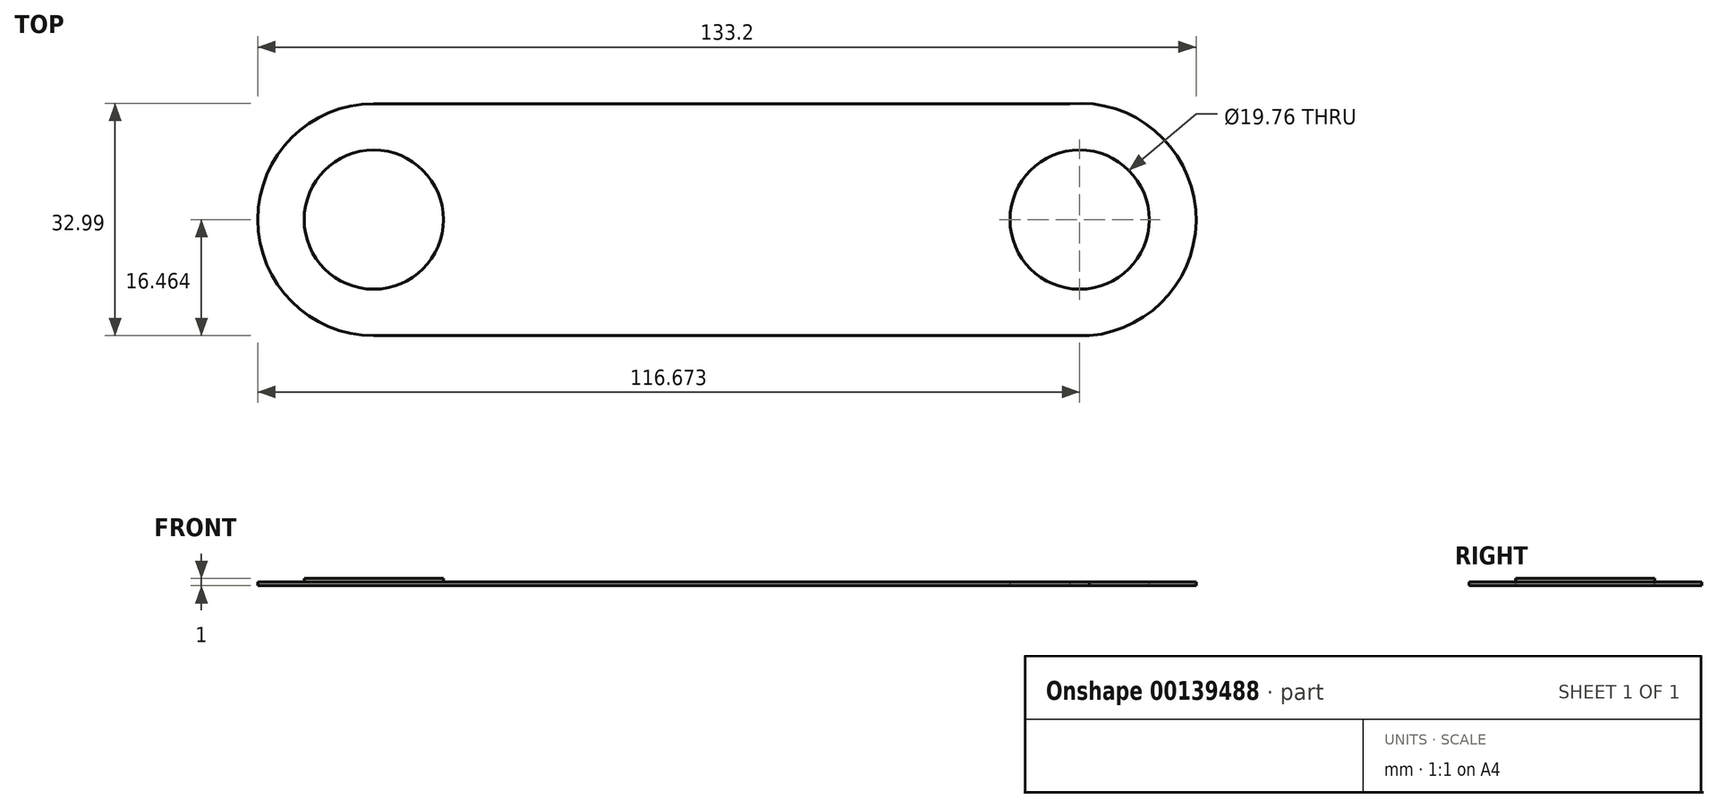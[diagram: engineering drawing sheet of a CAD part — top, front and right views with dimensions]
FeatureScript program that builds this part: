
annotation { "Feature Type Name" : "Feature", "Feature Type Description" : "" }
export const myFeature = defineFeature(function(context is Context, id is Id, definition is map)
    precondition{}
    {
        {
            assignVariable(context, id + "F0", {"name" : "Depth", "anyValue" : .5});
        }
        {
            var Q0;
            Q0=qCreatedBy(makeId("Top.planeOp"),FACE);
            var sketch = newSketch(context, id + "F1", { "sketchPlane" : qUnion([Q0])});
            skLineSegment(sketch, "E0.bottom", {"start": v(48, 16) * mm, "end": v(-50.8, 16) * mm});
            skLineSegment(sketch, "E0.top", {"start": v(50.8, -16.93) * mm, "end": v(-50.8, -16.93) * mm});
            skPoint(sketch, "E0.middle", {"position": v(0, 0) * mm});
            skArc(sketch, "E1", {"start": v(-50.8, 16) * mm, "mid": v(-67.27, -0.47) * mm, "end": v(-50.8, -16.93) * mm});
            skArc(sketch, "E2", {"start": v(48, 16) * mm, "mid": v(65.87, 0.93) * mm, "end": v(50.8, -16.93) * mm});
            skSolve(sketch);
        }
        {
            var Q0;
            Q0 = qSketchRegion(id + "F1", true);
            extrude(context, id + "F2", {"entities" : qUnion([Q0]), "depth" : (getVariable(context, 'Depth')) * mm});
        }
        {
            var Q0;
            Q0=makeQuery(id+"F2.opExtrude","CAP_FACE",FACE,{"disambiguationData":[OSD([sQuery(id+"F1.wireOp",EDGE,"E0.bottom"),sQuery(id+"F1.wireOp",EDGE,"E0.top"),sQuery(id+"F1.wireOp",EDGE,"E1"),sQuery(id+"F1.wireOp",EDGE,"E2")])],"isStart":false});
            var sketch = newSketch(context, id + "F3", { "sketchPlane" : qUnion([Q0])});
            skCircle(sketch, "E3", {"center": v(-50.8, -0.47) * mm, "radius": 9.88 * mm});
            skCircle(sketch, "E4", {"center": v(49.4, -0.47) * mm, "radius": 9.88 * mm});
            skSolve(sketch);
        }
        {
            var Q0;
            Q0=makeQuery(id+"F3.imprint","IMPRINT",FACE,{"disambiguationData":[TD([[makeQuery(id+"F3.imprint","IMPRINT",EDGE,{"derivedFrom":sQuery(id+"F3.wireOp",EDGE,"E3")}),1.0]])]});
            var Q1;
            Q1=sQuery(id+"F3.wireOp",EDGE,"E3");
            extrude(context, id + "F4", {"entities" : qUnion([Q0]), "operationType" : NewBodyOperationType.ADD, "surfaceEntities" : qUnion([Q1]), "depth" : (getVariable(context, 'Depth')) * mm});
        }
        {
            var Q0;
            Q0=makeQuery(id+"F3.imprint","IMPRINT",FACE,{"disambiguationData":[TD([[makeQuery(id+"F3.imprint","IMPRINT",EDGE,{"derivedFrom":sQuery(id+"F3.wireOp",EDGE,"E4")}),1.0]])]});
            extrude(context, id + "F5", {"entities" : qUnion([Q0]), "operationType" : NewBodyOperationType.REMOVE, "oppositeDirection" : true, "depth" : (getVariable(context, 'Depth')) * mm});
        }
    });
